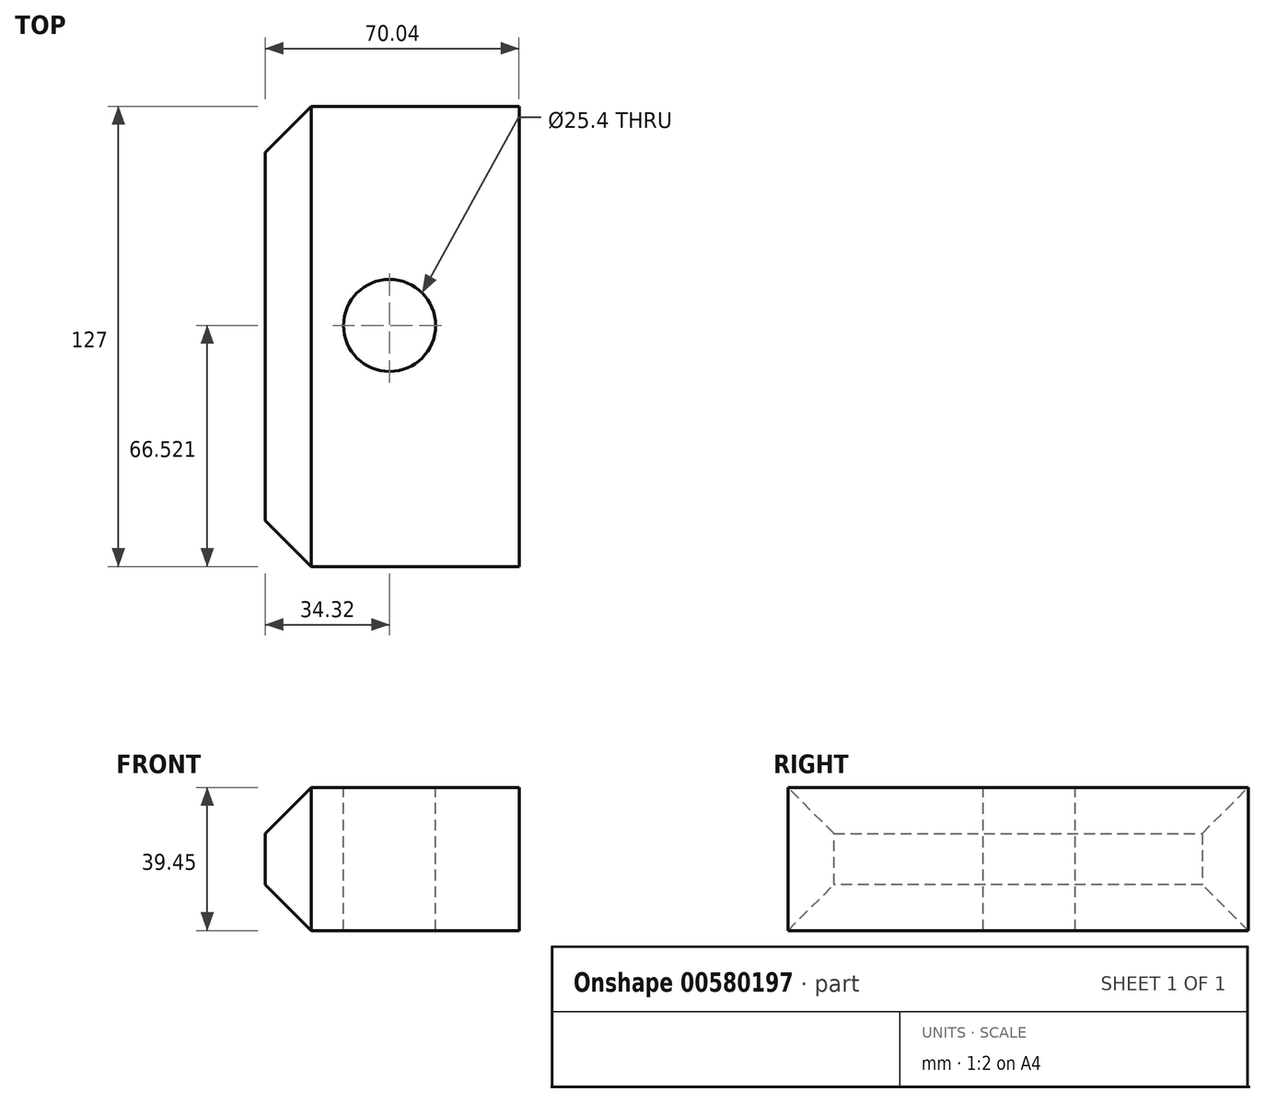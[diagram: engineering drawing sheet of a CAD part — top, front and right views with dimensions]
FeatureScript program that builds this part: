
annotation { "Feature Type Name" : "Feature", "Feature Type Description" : "" }
export const myFeature = defineFeature(function(context is Context, id is Id, definition is map)
    precondition{}
    {
        {
            var Q0;
            Q0=qCreatedBy(makeId("Front.planeOp"),FACE);
            var sketch = newSketch(context, id + "F0", { "sketchPlane" : qUnion([Q0])});
            skLineSegment(sketch, "E0", {"start": v(0, 0) * mm, "end": v(0, -39.45) * mm});
            skLineSegment(sketch, "E1", {"start": v(0, -39.45) * mm, "end": v(70.04, -39.45) * mm});
            skLineSegment(sketch, "E2", {"start": v(70.04, -39.45) * mm, "end": v(70.04, 0) * mm});
            skLineSegment(sketch, "E3", {"start": v(70.04, 0) * mm, "end": v(0, 0) * mm});
            skSolve(sketch);
        }
        {
            var Q0;
            Q0=makeQuery(id+"F0.imprint","IMPRINT",FACE,{"disambiguationData":[TD([[makeQuery(id+"F0.imprint","IMPRINT",EDGE,{"derivedFrom":sQuery(id+"F0.wireOp",EDGE,"E0")}),1.0]])]});
            extrude(context, id + "F1", {"entities" : qUnion([Q0]), "depth" : 127 * mm, "offsetDistance" : 25.4 * mm});
        }
        {
            var Q0;
            Q0=makeQuery(id+"F1.opExtrude","SWEPT_FACE",FACE,{"disambiguationData":[OSD([sQuery(id+"F0.wireOp",EDGE,"E3")])]});
            var sketch = newSketch(context, id + "F2", { "sketchPlane" : qUnion([Q0])});
            skPoint(sketch, "E4", {"position": v(34.32, -60.48) * mm});
            skSolve(sketch);
        }
        {
            var Q0;
            Q0=sQuery(id+"F2.wireOp",VERTEX,"E4");
            var Q1;
            Q1=makeQuery(id+"F1.opExtrude","SWEPT_BODY",BODY,{"disambiguationData":[OSD([sQuery(id+"F0.wireOp",EDGE,"E0"),sQuery(id+"F0.wireOp",EDGE,"E1"),sQuery(id+"F0.wireOp",EDGE,"E2"),sQuery(id+"F0.wireOp",EDGE,"E3")])]});
            hole(context, id + "F3", {"style" : HoleStyle.SIMPLE, "endStyle" : HoleEndStyle.THROUGH, "holeDiameter" : 25.4 * mm, "isTappedThrough" : true, "tappedDepth" : 12.7 * mm, "tapClearance" : 3, "locations" : qUnion([Q0]), "scope" : qUnion([Q1])});
        }
        {
            var Q0;
            Q0=makeQuery(id+"F1.opExtrude","SWEPT_FACE",FACE,{"disambiguationData":[OSD([sQuery(id+"F0.wireOp",EDGE,"E0")])]});
            chamfer(context, id + "F4", {"entities" : qUnion([Q0]), "width" : 12.7 * mm, "tangentPropagation" : true});
        }
    });
